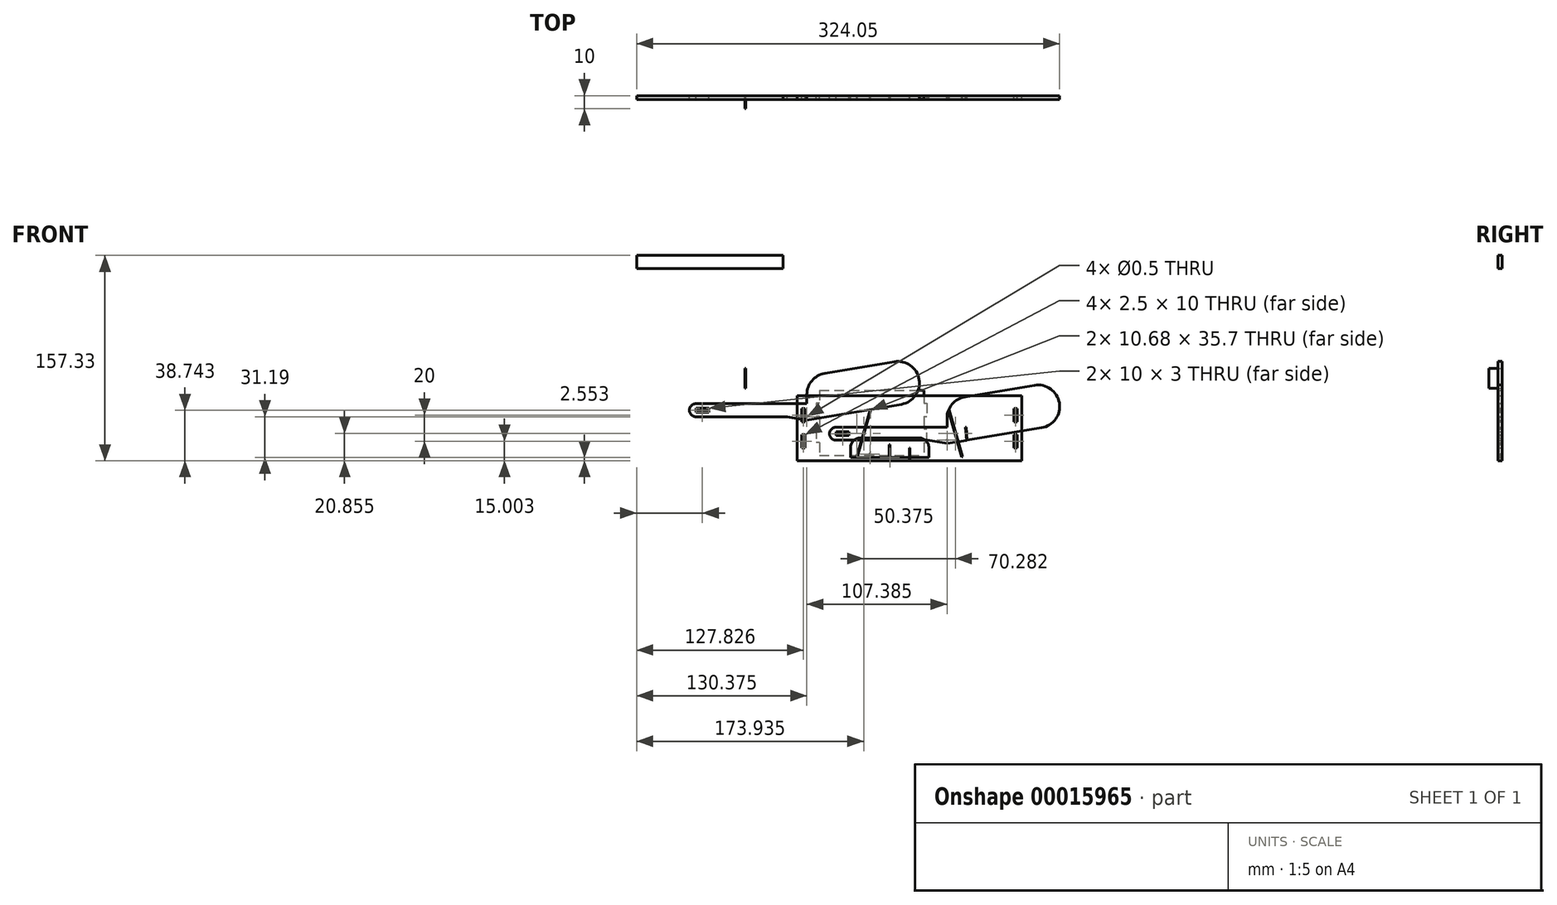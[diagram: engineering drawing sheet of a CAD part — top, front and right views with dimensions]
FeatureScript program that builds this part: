
annotation { "Feature Type Name" : "Feature", "Feature Type Description" : "" }
export const myFeature = defineFeature(function(context is Context, id is Id, definition is map)
    precondition{}
    {
        {
            var Q0;
            Q0=qCreatedBy(makeId("Front.planeOp"),FACE);
            var sketch = newSketch(context, id + "F0", { "sketchPlane" : qUnion([Q0])});
            skLineSegment(sketch, "E0.bottom", {"start": v(-60.78, 33.14) * mm, "end": v(19.22, 33.14) * mm});
            skLineSegment(sketch, "E0.top", {"start": v(-60.78, -16.86) * mm, "end": v(19.22, -16.86) * mm});
            skLineSegment(sketch, "E0.left", {"start": v(-60.78, 33.14) * mm, "end": v(-60.78, 23.14) * mm});
            skLineSegment(sketch, "E0.right", {"start": v(19.22, 33.14) * mm, "end": v(19.22, 23.14) * mm});
            skLineSegment(sketch, "E1.bottom", {"start": v(19.22, 23.14) * mm, "end": v(21.72, 23.14) * mm});
            skLineSegment(sketch, "E1.top", {"start": v(19.22, 13.14) * mm, "end": v(21.72, 13.14) * mm});
            skLineSegment(sketch, "E1.right", {"start": v(21.72, 23.14) * mm, "end": v(21.72, 13.14) * mm});
            skLineSegment(sketch, "E2.bottom", {"start": v(19.22, -6.86) * mm, "end": v(21.72, -6.86) * mm});
            skLineSegment(sketch, "E2.top", {"start": v(19.22, 3.5) * mm, "end": v(21.72, 3.5) * mm});
            skLineSegment(sketch, "E2.right", {"start": v(21.72, -6.86) * mm, "end": v(21.72, 3.5) * mm});
            skLineSegment(sketch, "E3.bottom", {"start": v(-60.78, 23.14) * mm, "end": v(-63.28, 23.14) * mm});
            skLineSegment(sketch, "E3.top", {"start": v(-60.78, 13.14) * mm, "end": v(-63.28, 13.14) * mm});
            skLineSegment(sketch, "E3.right", {"start": v(-63.28, 23.14) * mm, "end": v(-63.28, 13.14) * mm});
            skLineSegment(sketch, "E4.bottom", {"start": v(-60.78, 3.5) * mm, "end": v(-63.28, 3.5) * mm});
            skLineSegment(sketch, "E4.top", {"start": v(-60.78, -6.86) * mm, "end": v(-63.28, -6.86) * mm});
            skLineSegment(sketch, "E4.right", {"start": v(-63.28, 3.5) * mm, "end": v(-63.28, -6.86) * mm});
            skLineSegment(sketch, "E5.trimOffspring", {"start": v(-60.78, 13.14) * mm, "end": v(-60.78, 3.5) * mm});
            skLineSegment(sketch, "E6.trimOffspring", {"start": v(-60.78, -6.86) * mm, "end": v(-60.78, -16.86) * mm});
            skLineSegment(sketch, "E7.trimOffspring", {"start": v(19.22, 13.14) * mm, "end": v(19.22, 3.5) * mm});
            skLineSegment(sketch, "E8.trimOffspring", {"start": v(19.22, -6.86) * mm, "end": v(19.22, -16.86) * mm});
            skSolve(sketch);
        }
        {
            var Q0;
            Q0=makeQuery(id+"F0.imprint","IMPRINT",FACE,{"disambiguationData":[TD([[makeQuery(id+"F0.imprint","IMPRINT",EDGE,{"derivedFrom":sQuery(id+"F0.wireOp",EDGE,"E0.bottom")}),-1.0]])]});
            extrude(context, id + "F1", {"entities" : qUnion([Q0]), "depth" : 2.5 * mm});
        }
        {
            var Q0;
            Q0=qCreatedBy(makeId("Front.planeOp"),FACE);
            var sketch = newSketch(context, id + "F2", { "sketchPlane" : qUnion([Q0])});
            skLineSegment(sketch, "E9.bottom", {"start": v(-77.67, 29.16) * mm, "end": v(94.33, 29.16) * mm});
            skLineSegment(sketch, "E9.top", {"start": v(-77.67, -20.84) * mm, "end": v(8.1, -20.84) * mm});
            skLineSegment(sketch, "E9.left", {"start": v(-77.67, 29.16) * mm, "end": v(-77.67, -20.84) * mm});
            skLineSegment(sketch, "E9.right", {"start": v(94.33, 29.16) * mm, "end": v(94.33, -20.84) * mm});
            skLineSegment(sketch, "E10", {"start": v(-71.67, 29.16) * mm, "end": v(-71.67, -20.84) * mm, "construction": true});
            skLineSegment(sketch, "E11", {"start": v(88.33, -20.84) * mm, "end": v(88.33, 29.16) * mm, "construction": true});
            skLineSegment(sketch, "E12.bottom", {"start": v(88.33, 19.16) * mm, "end": v(90.83, 19.16) * mm});
            skLineSegment(sketch, "E12.top", {"start": v(88.33, 9.16) * mm, "end": v(90.83, 9.16) * mm});
            skLineSegment(sketch, "E12.left", {"start": v(88.33, 19.16) * mm, "end": v(88.33, 9.16) * mm});
            skLineSegment(sketch, "E12.right", {"start": v(90.83, 19.16) * mm, "end": v(90.83, 9.16) * mm});
            skLineSegment(sketch, "E13.bottom", {"start": v(88.33, -10.84) * mm, "end": v(90.83, -10.84) * mm});
            skLineSegment(sketch, "E13.top", {"start": v(88.33, -0.84) * mm, "end": v(90.83, -0.84) * mm});
            skLineSegment(sketch, "E13.left", {"start": v(88.33, -10.84) * mm, "end": v(88.33, -0.84) * mm});
            skLineSegment(sketch, "E13.right", {"start": v(90.83, -10.84) * mm, "end": v(90.83, -0.84) * mm});
            skLineSegment(sketch, "E14.bottom", {"start": v(-71.67, 19.16) * mm, "end": v(-74.17, 19.16) * mm});
            skLineSegment(sketch, "E14.top", {"start": v(-71.67, 9.16) * mm, "end": v(-74.17, 9.16) * mm});
            skLineSegment(sketch, "E14.left", {"start": v(-71.67, 19.16) * mm, "end": v(-71.67, 9.16) * mm});
            skLineSegment(sketch, "E14.right", {"start": v(-74.17, 19.16) * mm, "end": v(-74.17, 9.16) * mm});
            skLineSegment(sketch, "E15.bottom", {"start": v(-71.67, -10.84) * mm, "end": v(-74.17, -10.84) * mm});
            skLineSegment(sketch, "E15.top", {"start": v(-71.67, -0.84) * mm, "end": v(-74.17, -0.84) * mm});
            skLineSegment(sketch, "E15.left", {"start": v(-71.67, -10.84) * mm, "end": v(-71.67, -0.84) * mm});
            skLineSegment(sketch, "E15.right", {"start": v(-74.17, -10.84) * mm, "end": v(-74.17, -0.84) * mm});
            skLineSegment(sketch, "E16", {"start": v(8.33, -20.84) * mm, "end": v(8.33, 29.16) * mm, "construction": true});
            skLineSegment(sketch, "E17.rect.top", {"start": v(8.55, -10.84) * mm, "end": v(8.1, -10.84) * mm});
            skLineSegment(sketch, "E17.rect.left", {"start": v(8.55, -20.84) * mm, "end": v(8.55, -10.84) * mm});
            skLineSegment(sketch, "E17.rect.right", {"start": v(8.1, -20.84) * mm, "end": v(8.1, -10.84) * mm});
            skPoint(sketch, "E17.rect.middle", {"position": v(8.33, -15.84) * mm});
            skLineSegment(sketch, "E18.trimOffspring", {"start": v(8.55, -20.84) * mm, "end": v(94.33, -20.84) * mm});
            skPoint(sketch, "E19", {"position": v(-31.67, -20.84) * mm});
            skPoint(sketch, "E20", {"position": v(48.33, -20.84) * mm});
            skLineSegment(sketch, "E21", {"start": v(-31.67, -20.84) * mm, "end": v(-31.67, 29.16) * mm, "construction": true});
            skLineSegment(sketch, "E22", {"start": v(48.33, -20.84) * mm, "end": v(48.33, 29.16) * mm, "construction": true});
            skLineSegment(sketch, "E23.bottom", {"start": v(-31.67, -17.84) * mm, "end": v(-21.48, 17.73) * mm});
            skLineSegment(sketch, "E23.top", {"start": v(-32.15, -17.7) * mm, "end": v(-21.96, 17.87) * mm});
            skLineSegment(sketch, "E23.left", {"start": v(-31.67, -17.84) * mm, "end": v(-32.15, -17.7) * mm});
            skLineSegment(sketch, "E23.right", {"start": v(-21.48, 17.73) * mm, "end": v(-21.96, 17.87) * mm});
            skLineSegment(sketch, "E24.MirrorCS", {"start": v(88.1, -20.84) * mm, "end": v(2.33, -20.84) * mm});
            skLineSegment(sketch, "E25.MirrorCS", {"start": v(38.13, 17.73) * mm, "end": v(38.6, 17.87) * mm});
            skLineSegment(sketch, "E26.MirrorCS", {"start": v(48.33, -17.84) * mm, "end": v(48.8, -17.7) * mm});
            skLineSegment(sketch, "E27.MirrorCS", {"start": v(48.8, -17.7) * mm, "end": v(38.6, 17.87) * mm});
            skLineSegment(sketch, "E28.MirrorCS", {"start": v(48.33, -17.84) * mm, "end": v(38.13, 17.73) * mm});
            skLineSegment(sketch, "E29", {"start": v(-6.67, -20.84) * mm, "end": v(-6.67, -18.29) * mm, "construction": true});
            skLineSegment(sketch, "E30", {"start": v(-6.67, -18.29) * mm, "end": v(8.33, -18.29) * mm, "construction": true});
            skCircle(sketch, "E31", {"center": v(-6.67, -18.29) * mm, "radius": 0.25 * mm});
            skSolve(sketch);
        }
        {
            var Q0;
            Q0=makeQuery(id+"F2.imprint","IMPRINT",FACE,{"disambiguationData":[TD([[makeQuery(id+"F2.imprint","IMPRINT",EDGE,{"derivedFrom":sQuery(id+"F2.wireOp",EDGE,"E9.bottom")}),-1.0]])]});
            extrude(context, id + "F3", {"entities" : qUnion([Q0]), "depth" : 3 * mm});
        }
        {
            var Q0;
            Q0=qCreatedBy(makeId("Front.planeOp"),FACE);
            var sketch = newSketch(context, id + "F4", { "sketchPlane" : qUnion([Q0])});
            skLineSegment(sketch, "E32.bottom", {"start": v(-36.86, -18.3) * mm, "end": v(-7.16, -18.3) * mm});
            skLineSegment(sketch, "E32.top", {"start": v(-36.86, -3.3) * mm, "end": v(-36.86, -3.3) * mm});
            skLineSegment(sketch, "E32.left", {"start": v(-36.86, -18.3) * mm, "end": v(-36.86, -10.8) * mm});
            skLineSegment(sketch, "E32.right", {"start": v(23.14, -18.3) * mm, "end": v(23.14, -10.8) * mm});
            skLineSegment(sketch, "E33", {"start": v(-6.86, -3.3) * mm, "end": v(-6.86, -18.3) * mm, "construction": true});
            skLineSegment(sketch, "E34.rect.bottom", {"start": v(-7.16, -18.3) * mm, "end": v(-7.16, -18.3) * mm});
            skLineSegment(sketch, "E34.rect.top", {"start": v(-7.16, -8.3) * mm, "end": v(-6.56, -8.3) * mm});
            skLineSegment(sketch, "E34.rect.left", {"start": v(-7.16, -18.3) * mm, "end": v(-7.16, -8.3) * mm});
            skLineSegment(sketch, "E34.rect.right", {"start": v(-6.56, -18.3) * mm, "end": v(-6.56, -8.3) * mm});
            skPoint(sketch, "E34.rect.middle", {"position": v(-6.86, -13.3) * mm});
            skLineSegment(sketch, "E35", {"start": v(-6.86, -15.76) * mm, "end": v(-21.86, -15.76) * mm, "construction": true});
            skLineSegment(sketch, "E36", {"start": v(-21.86, -15.76) * mm, "end": v(-21.86, -18.3) * mm, "construction": true});
            skCircle(sketch, "E37", {"center": v(-21.86, -15.76) * mm, "radius": 0.25 * mm});
            skLineSegment(sketch, "E38", {"start": v(-36.86, -10.8) * mm, "end": v(23.14, -10.8) * mm, "construction": true});
            skPoint(sketch, "E39", {"position": v(-29.36, -3.3) * mm});
            skPoint(sketch, "E40", {"position": v(15.64, -3.3) * mm});
            skPoint(sketch, "E41", {"position": v(-36.86, -10.8) * mm});
            skPoint(sketch, "E42", {"position": v(23.14, -10.8) * mm});
            skLineSegment(sketch, "E43", {"start": v(23.14, -10.8) * mm, "end": v(23.14, -3.3) * mm});
            skArc(sketch, "E44", {"start": v(15.64, -3.3) * mm, "mid": v(10.33, -16.1) * mm, "end": v(23.14, -10.8) * mm, "construction": true});
            skArc(sketch, "E45", {"start": v(23.14, -10.8) * mm, "mid": v(20.94, -5.5) * mm, "end": v(15.64, -3.3) * mm});
            skLineSegment(sketch, "E46", {"start": v(-36.86, -10.8) * mm, "end": v(-36.86, -3.3) * mm, "construction": true});
            skArc(sketch, "E47", {"start": v(-29.36, -3.3) * mm, "mid": v(-34.67, -5.5) * mm, "end": v(-36.86, -10.8) * mm});
            skArc(sketch, "E48", {"start": v(-36.86, -10.8) * mm, "mid": v(-24.06, -16.1) * mm, "end": v(-29.36, -3.3) * mm, "construction": true});
            skLineSegment(sketch, "E49", {"start": v(-29.36, -3.3) * mm, "end": v(-29.36, -3.3) * mm});
            skLineSegment(sketch, "E50", {"start": v(-36.86, -3.3) * mm, "end": v(-29.36, -3.3) * mm, "construction": true});
            skLineSegment(sketch, "E51", {"start": v(-29.36, -3.3) * mm, "end": v(15.64, -3.3) * mm});
            skLineSegment(sketch, "E52", {"start": v(23.14, -3.3) * mm, "end": v(23.14, -3.3) * mm});
            skLineSegment(sketch, "E53", {"start": v(15.64, -3.3) * mm, "end": v(23.14, -3.3) * mm, "construction": true});
            skLineSegment(sketch, "E54", {"start": v(-7.16, -18.3) * mm, "end": v(-6.56, -18.3) * mm, "construction": true});
            skLineSegment(sketch, "E55", {"start": v(-6.56, -18.3) * mm, "end": v(-6.56, -18.3) * mm});
            skLineSegment(sketch, "E56", {"start": v(-6.56, -18.3) * mm, "end": v(23.14, -18.3) * mm});
            skSolve(sketch);
        }
        {
            var Q0;
            Q0=makeQuery(id+"F4.imprint","IMPRINT",FACE,{"disambiguationData":[TD([[makeQuery(id+"F4.imprint","IMPRINT",EDGE,{"derivedFrom":sQuery(id+"F4.wireOp",EDGE,"E32.bottom")}),1.0]])]});
            extrude(context, id + "F5", {"entities" : qUnion([Q0]), "depth" : 3 * mm});
        }
        {
            var Q0;
            Q0=qCreatedBy(makeId("Front.planeOp"),FACE);
            var sketch = newSketch(context, id + "F6", { "sketchPlane" : qUnion([Q0])});
            skLineSegment(sketch, "E57.bottom", {"start": v(-200.75, 136.49) * mm, "end": v(-88.75, 136.49) * mm});
            skLineSegment(sketch, "E57.top", {"start": v(-200.75, 126.49) * mm, "end": v(-88.75, 126.49) * mm});
            skLineSegment(sketch, "E57.left", {"start": v(-200.75, 136.49) * mm, "end": v(-200.75, 126.49) * mm});
            skLineSegment(sketch, "E57.right", {"start": v(-88.75, 136.49) * mm, "end": v(-88.75, 126.49) * mm});
            skSolve(sketch);
        }
        {
            var Q0;
            Q0 = qSketchRegion(id + "F6", true);
            extrude(context, id + "F7", {"entities" : qUnion([Q0]), "depth" : 3 * mm});
        }
        {
            var Q0;
            Q0=qCreatedBy(makeId("Front.planeOp"),FACE);
            var sketch = newSketch(context, id + "F8", { "sketchPlane" : qUnion([Q0])});
            skLineSegment(sketch, "E58.bottom", {"start": v(-48, 4.89) * mm, "end": v(37, 4.89) * mm});
            skLineSegment(sketch, "E58.top", {"start": v(-48, -5.11) * mm, "end": v(22, -5.11) * mm});
            skLineSegment(sketch, "E58.left", {"start": v(-48, 4.89) * mm, "end": v(-48, -5.11) * mm, "construction": true});
            skLineSegment(sketch, "E58.right", {"start": v(52, 4.89) * mm, "end": v(52, -5.11) * mm, "construction": true});
            skLineSegment(sketch, "E59", {"start": v(-48, -0.11) * mm, "end": v(52, -0.11) * mm, "construction": true});
            skLineSegment(sketch, "E60.rect.bottom", {"start": v(-48, 1.39) * mm, "end": v(-38, 1.39) * mm});
            skLineSegment(sketch, "E60.rect.top", {"start": v(-48, -1.61) * mm, "end": v(-38, -1.61) * mm});
            skLineSegment(sketch, "E60.rect.left", {"start": v(-48, 1.39) * mm, "end": v(-48, -1.61) * mm});
            skLineSegment(sketch, "E60.rect.right", {"start": v(-38, 1.39) * mm, "end": v(-38, -1.61) * mm});
            skPoint(sketch, "E60.rect.middle", {"position": v(-43, -0.11) * mm});
            skPoint(sketch, "E61", {"position": v(22, -5.11) * mm});
            skLineSegment(sketch, "E62", {"start": v(52, -5.11) * mm, "end": v(52, -5.11) * mm});
            skLineSegment(sketch, "E63", {"start": v(37, -5.11) * mm, "end": v(52, -5.11) * mm, "construction": true});
            skLineSegment(sketch, "E64", {"start": v(22, -5.11) * mm, "end": v(37, -5.11) * mm, "construction": true});
            skLineSegment(sketch, "E65", {"start": v(37, -5.11) * mm, "end": v(37, -7.61) * mm, "construction": true});
            skLineSegment(sketch, "E66", {"start": v(22, -5.11) * mm, "end": v(37, -7.61) * mm});
            skLineSegment(sketch, "E67", {"start": v(37, -7.61) * mm, "end": v(37, -7.61) * mm});
            skCircle(sketch, "E68", {"center": v(37, -5.11) * mm, "radius": 0.25 * mm});
            skLineSegment(sketch, "E69", {"start": v(125.79, 7.18) * mm, "end": v(120.36, 39.73) * mm, "construction": true});
            skLineSegment(sketch, "E70", {"start": v(120.36, 39.73) * mm, "end": v(120.36, 39.73) * mm});
            skLineSegment(sketch, "E71", {"start": v(37, -5.11) * mm, "end": v(37, 34.55) * mm, "construction": true});
            skLineSegment(sketch, "E72", {"start": v(123.07, 23.46) * mm, "end": v(37, 9.11) * mm, "construction": true});
            skLineSegment(sketch, "E73", {"start": v(37, 4.89) * mm, "end": v(37, 11.86) * mm});
            skArc(sketch, "E74", {"start": v(-48, 4.89) * mm, "mid": v(-53, -0.11) * mm, "end": v(-48, -5.11) * mm});
            skArc(sketch, "E75", {"start": v(-48, -5.11) * mm, "mid": v(-43, -0.11) * mm, "end": v(-48, 4.89) * mm, "construction": true});
            skLineSegment(sketch, "E76", {"start": v(52, 4.89) * mm, "end": v(52, 4.89) * mm});
            skLineSegment(sketch, "E77", {"start": v(37, 4.89) * mm, "end": v(52, 4.89) * mm, "construction": true});
            skArc(sketch, "E78", {"start": v(37, 11.86) * mm, "mid": v(42.84, -0.72) * mm, "end": v(56.22, -4.41) * mm, "construction": true});
            skArc(sketch, "E79", {"start": v(56.22, -4.41) * mm, "mid": v(69.79, 14.58) * mm, "end": v(50.8, 28.14) * mm, "construction": true});
            skArc(sketch, "E80", {"start": v(104.08, 37.02) * mm, "mid": v(90.52, 18.03) * mm, "end": v(109.5, 4.47) * mm, "construction": true});
            skArc(sketch, "E81", {"start": v(109.5, 4.47) * mm, "mid": v(123.07, 23.46) * mm, "end": v(104.08, 37.02) * mm});
            skLineSegment(sketch, "E82", {"start": v(120.36, 39.73) * mm, "end": v(104.08, 37.02) * mm, "construction": true});
            skLineSegment(sketch, "E83", {"start": v(104.08, 37.02) * mm, "end": v(50.8, 28.14) * mm});
            skLineSegment(sketch, "E84", {"start": v(125.79, 7.18) * mm, "end": v(125.79, 7.18) * mm});
            skLineSegment(sketch, "E85", {"start": v(109.5, 4.47) * mm, "end": v(125.79, 7.18) * mm, "construction": true});
            skArc(sketch, "E86", {"start": v(50.8, 28.14) * mm, "mid": v(40.92, 22.53) * mm, "end": v(37, 11.86) * mm});
            skLineSegment(sketch, "E87", {"start": v(37, 11.86) * mm, "end": v(37, 11.86) * mm});
            skLineSegment(sketch, "E88", {"start": v(52, -5.11) * mm, "end": v(52, -2.11) * mm, "construction": true});
            skLineSegment(sketch, "E89", {"start": v(51.17, 4.84) * mm, "end": v(51.76, 4.89) * mm});
            skLineSegment(sketch, "E90", {"start": v(51.76, 4.89) * mm, "end": v(52.54, -5.02) * mm});
            skLineSegment(sketch, "E91", {"start": v(51.47, 4.87) * mm, "end": v(52, -2.11) * mm, "construction": true});
            skLineSegment(sketch, "E92", {"start": v(51.94, -5.12) * mm, "end": v(51.17, 4.84) * mm});
            skLineSegment(sketch, "E93", {"start": v(52.54, -5.02) * mm, "end": v(109.5, 4.47) * mm});
            skLineSegment(sketch, "E94", {"start": v(51.94, -5.12) * mm, "end": v(52.54, -5.02) * mm, "construction": true});
            skLineSegment(sketch, "E95", {"start": v(51.94, -5.12) * mm, "end": v(51.94, -5.12) * mm});
            skLineSegment(sketch, "E96", {"start": v(51.94, -5.12) * mm, "end": v(52, -5.11) * mm});
            skLineSegment(sketch, "E97", {"start": v(37, -7.61) * mm, "end": v(51.94, -5.12) * mm});
            skLineSegment(sketch, "E98", {"start": v(51.94, -5.12) * mm, "end": v(52, -5.11) * mm, "construction": true});
            skSolve(sketch);
        }
        {
            var Q0;
            Q0=makeQuery(id+"F8.imprint","IMPRINT",FACE,{"disambiguationData":[TD([[makeQuery(id+"F8.imprint","IMPRINT",EDGE,{"derivedFrom":sQuery(id+"F8.wireOp",EDGE,"E58.bottom")}),-1.0]])]});
            extrude(context, id + "F9", {"entities" : qUnion([Q0]), "depth" : 3 * mm});
        }
        {
            var Q0;
            Q0=qCreatedBy(makeId("Front.planeOp"),FACE);
            var sketch = newSketch(context, id + "F10", { "sketchPlane" : qUnion([Q0])});
            skLineSegment(sketch, "E99.bottom", {"start": v(-155.38, 22.9) * mm, "end": v(-70.38, 22.9) * mm});
            skLineSegment(sketch, "E99.top", {"start": v(-155.38, 12.9) * mm, "end": v(-85.38, 12.9) * mm});
            skLineSegment(sketch, "E99.left", {"start": v(-155.38, 22.9) * mm, "end": v(-155.38, 12.9) * mm, "construction": true});
            skLineSegment(sketch, "E99.right", {"start": v(-55.38, 22.9) * mm, "end": v(-55.38, 12.9) * mm, "construction": true});
            skLineSegment(sketch, "E100", {"start": v(-155.38, 17.9) * mm, "end": v(-55.38, 17.9) * mm, "construction": true});
            skLineSegment(sketch, "E101.rect.bottom", {"start": v(-155.38, 19.4) * mm, "end": v(-145.38, 19.4) * mm});
            skLineSegment(sketch, "E101.rect.top", {"start": v(-155.38, 16.4) * mm, "end": v(-145.38, 16.4) * mm});
            skLineSegment(sketch, "E101.rect.left", {"start": v(-155.38, 19.4) * mm, "end": v(-155.38, 16.4) * mm});
            skLineSegment(sketch, "E101.rect.right", {"start": v(-145.38, 19.4) * mm, "end": v(-145.38, 16.4) * mm});
            skPoint(sketch, "E101.rect.middle", {"position": v(-150.38, 17.9) * mm});
            skPoint(sketch, "E102", {"position": v(-85.38, 12.9) * mm});
            skLineSegment(sketch, "E103", {"start": v(-55.38, 12.9) * mm, "end": v(-55.38, 12.9) * mm});
            skLineSegment(sketch, "E104", {"start": v(-70.38, 12.9) * mm, "end": v(-55.38, 12.9) * mm, "construction": true});
            skLineSegment(sketch, "E105", {"start": v(-85.38, 12.9) * mm, "end": v(-70.38, 12.9) * mm, "construction": true});
            skLineSegment(sketch, "E106", {"start": v(-70.38, 12.9) * mm, "end": v(-70.38, 10.4) * mm, "construction": true});
            skLineSegment(sketch, "E107", {"start": v(-85.38, 12.9) * mm, "end": v(-70.38, 10.4) * mm});
            skLineSegment(sketch, "E108", {"start": v(-70.38, 10.4) * mm, "end": v(-70.38, 10.4) * mm});
            skCircle(sketch, "E109", {"center": v(-70.38, 12.9) * mm, "radius": 0.25 * mm});
            skLineSegment(sketch, "E110", {"start": v(18.4, 25.2) * mm, "end": v(12.97, 57.75) * mm, "construction": true});
            skLineSegment(sketch, "E111", {"start": v(12.97, 57.75) * mm, "end": v(12.97, 57.75) * mm});
            skLineSegment(sketch, "E112", {"start": v(-70.38, 12.9) * mm, "end": v(-70.38, 52.57) * mm, "construction": true});
            skLineSegment(sketch, "E113", {"start": v(15.69, 41.47) * mm, "end": v(-70.38, 27.13) * mm, "construction": true});
            skLineSegment(sketch, "E114", {"start": v(-70.38, 22.9) * mm, "end": v(-70.38, 29.88) * mm});
            skArc(sketch, "E115", {"start": v(-155.38, 22.9) * mm, "mid": v(-160.38, 17.9) * mm, "end": v(-155.38, 12.9) * mm});
            skArc(sketch, "E116", {"start": v(-155.38, 12.9) * mm, "mid": v(-150.38, 17.9) * mm, "end": v(-155.38, 22.9) * mm, "construction": true});
            skLineSegment(sketch, "E117", {"start": v(-55.38, 22.9) * mm, "end": v(-55.38, 22.9) * mm});
            skLineSegment(sketch, "E118", {"start": v(-70.38, 22.9) * mm, "end": v(-55.38, 22.9) * mm, "construction": true});
            skArc(sketch, "E119", {"start": v(-70.38, 29.88) * mm, "mid": v(-64.54, 17.3) * mm, "end": v(-51.16, 13.6) * mm, "construction": true});
            skArc(sketch, "E120", {"start": v(-51.16, 13.6) * mm, "mid": v(-37.6, 32.6) * mm, "end": v(-56.59, 46.16) * mm, "construction": true});
            skArc(sketch, "E121", {"start": v(-3.3, 55.04) * mm, "mid": v(-16.86, 36.05) * mm, "end": v(2.12, 22.49) * mm, "construction": true});
            skArc(sketch, "E122", {"start": v(2.12, 22.49) * mm, "mid": v(15.69, 41.47) * mm, "end": v(-3.3, 55.04) * mm});
            skLineSegment(sketch, "E123", {"start": v(12.97, 57.75) * mm, "end": v(-3.3, 55.04) * mm, "construction": true});
            skLineSegment(sketch, "E124", {"start": v(-3.3, 55.04) * mm, "end": v(-56.59, 46.16) * mm});
            skLineSegment(sketch, "E125", {"start": v(18.4, 25.2) * mm, "end": v(18.4, 25.2) * mm});
            skLineSegment(sketch, "E126", {"start": v(2.12, 22.49) * mm, "end": v(18.4, 25.2) * mm, "construction": true});
            skArc(sketch, "E127", {"start": v(-56.59, 46.16) * mm, "mid": v(-66.47, 40.55) * mm, "end": v(-70.38, 29.88) * mm});
            skLineSegment(sketch, "E128", {"start": v(-70.38, 29.88) * mm, "end": v(-70.38, 29.88) * mm});
            skLineSegment(sketch, "E129", {"start": v(-55.38, 12.9) * mm, "end": v(-55.38, 15.9) * mm, "construction": true});
            skLineSegment(sketch, "E130", {"start": v(-56.22, 22.86) * mm, "end": v(-55.62, 22.9) * mm, "construction": true});
            skLineSegment(sketch, "E131", {"start": v(-55.62, 22.9) * mm, "end": v(-54.85, 13) * mm, "construction": true});
            skLineSegment(sketch, "E132", {"start": v(-55.92, 22.88) * mm, "end": v(-55.38, 15.9) * mm, "construction": true});
            skLineSegment(sketch, "E133", {"start": v(-55.44, 12.9) * mm, "end": v(-56.22, 22.86) * mm, "construction": true});
            skLineSegment(sketch, "E134", {"start": v(-54.85, 13) * mm, "end": v(2.12, 22.49) * mm});
            skLineSegment(sketch, "E135", {"start": v(-55.44, 12.9) * mm, "end": v(-54.85, 13) * mm});
            skLineSegment(sketch, "E136", {"start": v(-55.44, 12.9) * mm, "end": v(-55.44, 12.9) * mm});
            skLineSegment(sketch, "E137", {"start": v(-55.44, 12.9) * mm, "end": v(-55.38, 12.9) * mm});
            skLineSegment(sketch, "E138", {"start": v(-70.38, 10.4) * mm, "end": v(-55.44, 12.9) * mm});
            skLineSegment(sketch, "E139", {"start": v(-55.44, 12.9) * mm, "end": v(-55.38, 12.9) * mm, "construction": true});
            skSolve(sketch);
        }
        {
            var Q0;
            Q0=makeQuery(id+"F10.imprint","IMPRINT",FACE,{"disambiguationData":[TD([[makeQuery(id+"F10.imprint","IMPRINT",EDGE,{"derivedFrom":sQuery(id+"F10.wireOp",EDGE,"E99.bottom")}),-1.0]])]});
            extrude(context, id + "F11", {"entities" : qUnion([Q0]), "depth" : 3 * mm});
        }
        {
            var Q0;
            Q0=qCreatedBy(makeId("Front.planeOp"),FACE);
            var sketch = newSketch(context, id + "F12", { "sketchPlane" : qUnion([Q0])});
            skLineSegment(sketch, "E140.bottom", {"start": v(-117.65, 49.87) * mm, "end": v(-117.2, 49.87) * mm});
            skLineSegment(sketch, "E140.top", {"start": v(-117.65, 34.87) * mm, "end": v(-117.2, 34.87) * mm});
            skLineSegment(sketch, "E140.left", {"start": v(-117.65, 49.87) * mm, "end": v(-117.65, 34.87) * mm});
            skLineSegment(sketch, "E140.right", {"start": v(-117.2, 49.87) * mm, "end": v(-117.2, 34.87) * mm});
            skSolve(sketch);
        }
        {
            var Q0;
            Q0=makeQuery(id+"F12.imprint","IMPRINT",FACE,{"disambiguationData":[TD([[makeQuery(id+"F12.imprint","IMPRINT",EDGE,{"derivedFrom":sQuery(id+"F12.wireOp",EDGE,"E140.bottom")}),-1.0]])]});
            extrude(context, id + "F13", {"entities" : qUnion([Q0]), "depth" : 10 * mm});
        }
    });
